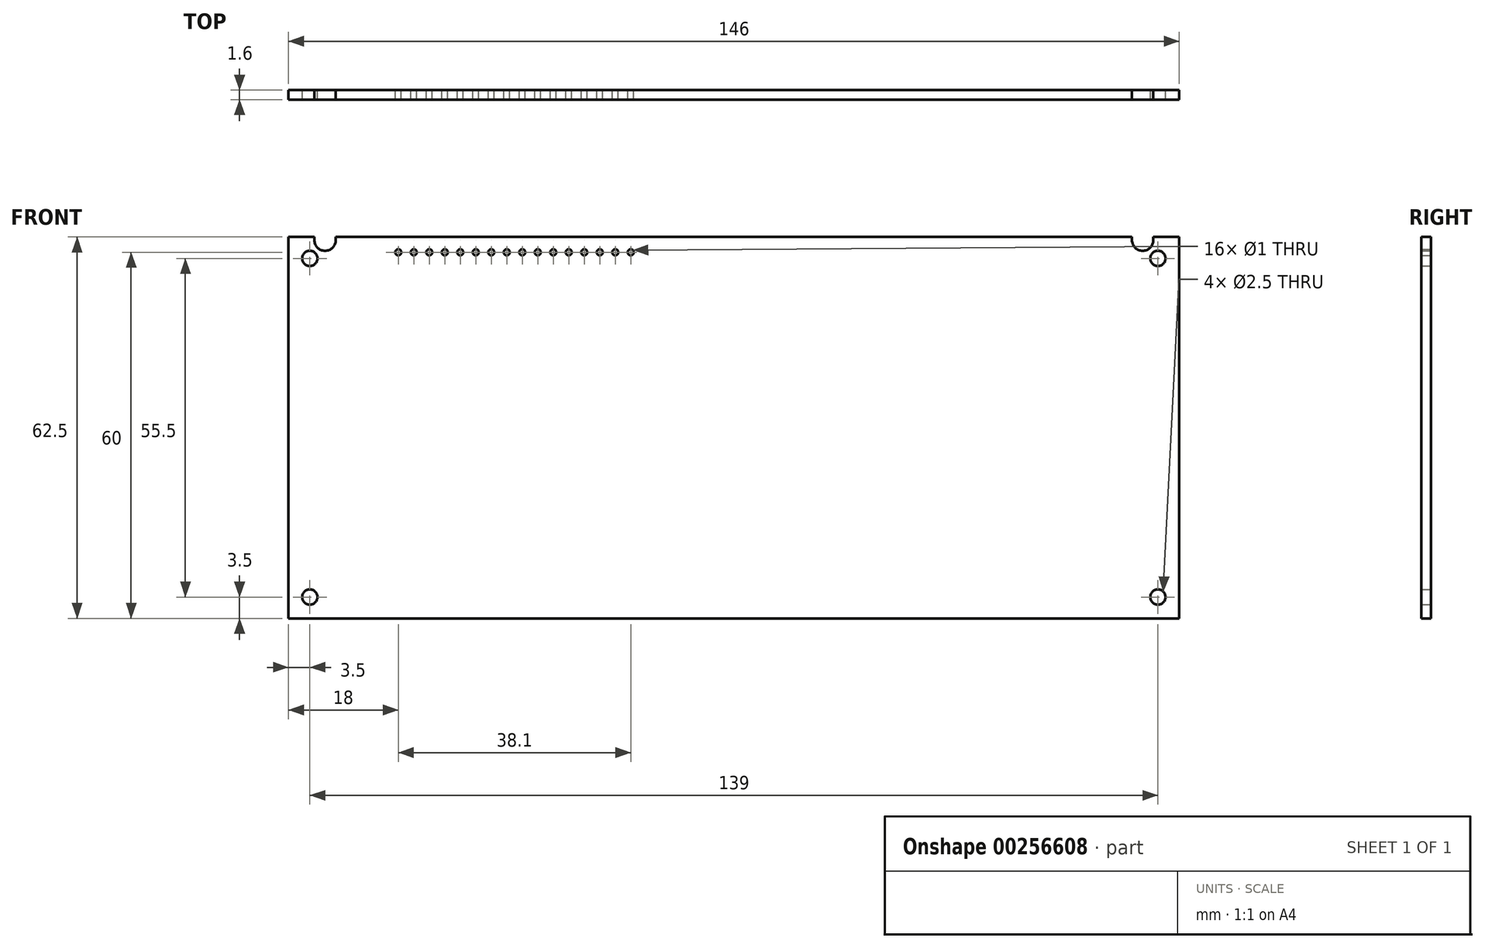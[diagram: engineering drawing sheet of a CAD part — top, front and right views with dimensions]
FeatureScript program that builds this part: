
annotation { "Feature Type Name" : "Feature", "Feature Type Description" : "" }
export const myFeature = defineFeature(function(context is Context, id is Id, definition is map)
    precondition{}
    {
        {
            var Q0;
            Q0=qCreatedBy(makeId("Front.planeOp"),FACE);
            var sketch = newSketch(context, id + "F0", { "sketchPlane" : qUnion([Q0])});
            skLineSegment(sketch, "E0.bottom", {"start": v(73, -31.25) * mm, "end": v(-73, -31.25) * mm});
            skLineSegment(sketch, "E0.top", {"start": v(73, 31.25) * mm, "end": v(-73, 31.25) * mm});
            skLineSegment(sketch, "E0.left", {"start": v(73, -31.25) * mm, "end": v(73, 31.25) * mm});
            skLineSegment(sketch, "E0.right", {"start": v(-73, -31.25) * mm, "end": v(-73, 31.25) * mm});
            skPoint(sketch, "E0.middle", {"position": v(0, 0) * mm});
            skCircle(sketch, "E1", {"center": v(-69.5, -27.75) * mm, "radius": 1.25 * mm});
            skCircle(sketch, "E2", {"center": v(69.5, -27.75) * mm, "radius": 1.25 * mm});
            skCircle(sketch, "E3", {"center": v(69.5, 27.75) * mm, "radius": 1.25 * mm});
            skCircle(sketch, "E4", {"center": v(-69.5, 27.75) * mm, "radius": 1.25 * mm});
            skLineSegment(sketch, "E5.bottom", {"start": v(-67, 29) * mm, "end": v(-67, 29) * mm});
            skLineSegment(sketch, "E5.top", {"start": v(-65.25, 33.5) * mm, "end": v(-68.75, 33.5) * mm});
            skLineSegment(sketch, "E5.left", {"start": v(-65.25, 30.75) * mm, "end": v(-65.25, 33.5) * mm});
            skLineSegment(sketch, "E5.right", {"start": v(-68.75, 30.75) * mm, "end": v(-68.75, 33.5) * mm});
            skPoint(sketch, "E5.middle", {"position": v(-67, 31.25) * mm});
            skLineSegment(sketch, "E6.bottom", {"start": v(67, 29) * mm, "end": v(67, 29) * mm});
            skLineSegment(sketch, "E6.top", {"start": v(68.75, 33.5) * mm, "end": v(65.25, 33.5) * mm});
            skLineSegment(sketch, "E6.left", {"start": v(68.75, 30.75) * mm, "end": v(68.75, 33.5) * mm});
            skLineSegment(sketch, "E6.right", {"start": v(65.25, 30.75) * mm, "end": v(65.25, 33.5) * mm});
            skPoint(sketch, "E6.middle", {"position": v(67, 31.25) * mm});
            skPoint(sketch, "E7.visualSharp", {"position": v(-68.75, 29) * mm});
            skArc(sketch, "E7.filletArc", {"start": v(-68.75, 30.75) * mm, "mid": v(-68.24, 29.51) * mm, "end": v(-67, 29) * mm});
            skPoint(sketch, "E8.visualSharp", {"position": v(-65.25, 29) * mm});
            skArc(sketch, "E8.filletArc", {"start": v(-67, 29) * mm, "mid": v(-65.76, 29.51) * mm, "end": v(-65.25, 30.75) * mm});
            skPoint(sketch, "E9.visualSharp", {"position": v(65.25, 29) * mm});
            skArc(sketch, "E9.filletArc", {"start": v(65.25, 30.75) * mm, "mid": v(65.76, 29.51) * mm, "end": v(67, 29) * mm});
            skPoint(sketch, "E10.visualSharp", {"position": v(68.75, 29) * mm});
            skArc(sketch, "E10.filletArc", {"start": v(67, 29) * mm, "mid": v(68.24, 29.51) * mm, "end": v(68.75, 30.75) * mm});
            skLineSegment(sketch, "E11", {"start": v(-55, 28.75) * mm, "end": v(-16.9, 28.75) * mm, "construction": true});
            skCircle(sketch, "E12", {"center": v(-55, 28.75) * mm, "radius": 0.5 * mm});
            skCircle(sketch, "E13", {"center": v(-52.46, 28.75) * mm, "radius": 0.5 * mm});
            skCircle(sketch, "E14", {"center": v(-47.38, 28.75) * mm, "radius": 0.5 * mm});
            skCircle(sketch, "E15", {"center": v(-49.92, 28.75) * mm, "radius": 0.5 * mm});
            skCircle(sketch, "E16", {"center": v(-37.22, 28.75) * mm, "radius": 0.5 * mm});
            skCircle(sketch, "E17", {"center": v(-39.76, 28.75) * mm, "radius": 0.5 * mm});
            skCircle(sketch, "E18", {"center": v(-44.84, 28.75) * mm, "radius": 0.5 * mm});
            skCircle(sketch, "E19", {"center": v(-42.3, 28.75) * mm, "radius": 0.5 * mm});
            skCircle(sketch, "E20", {"center": v(-34.68, 28.75) * mm, "radius": 0.5 * mm});
            skCircle(sketch, "E21", {"center": v(-32.14, 28.75) * mm, "radius": 0.5 * mm});
            skCircle(sketch, "E22", {"center": v(-29.6, 28.75) * mm, "radius": 0.5 * mm});
            skCircle(sketch, "E23", {"center": v(-21.98, 28.75) * mm, "radius": 0.5 * mm});
            skCircle(sketch, "E24", {"center": v(-24.52, 28.75) * mm, "radius": 0.5 * mm});
            skCircle(sketch, "E25", {"center": v(-27.06, 28.75) * mm, "radius": 0.5 * mm});
            skCircle(sketch, "E26", {"center": v(-19.44, 28.75) * mm, "radius": 0.5 * mm});
            skCircle(sketch, "E27", {"center": v(-16.9, 28.75) * mm, "radius": 0.5 * mm});
            skCircle(sketch, "E28", {"center": v(-69.5, 27.75) * mm, "radius": 2 * mm});
            skCircle(sketch, "E29", {"center": v(69.5, 27.75) * mm, "radius": 2 * mm});
            skCircle(sketch, "E30", {"center": v(69.5, -27.75) * mm, "radius": 2 * mm});
            skCircle(sketch, "E31", {"center": v(-69.5, -27.75) * mm, "radius": 2 * mm});
            skLineSegment(sketch, "E32.bottom", {"start": v(-55, 27.85) * mm, "end": v(-55, 27.85) * mm});
            skLineSegment(sketch, "E32.top", {"start": v(-54.1, 29.65) * mm, "end": v(-55.9, 29.65) * mm, "construction": true});
            skLineSegment(sketch, "E32.left", {"start": v(-54.1, 28.75) * mm, "end": v(-54.1, 29.65) * mm});
            skLineSegment(sketch, "E32.right", {"start": v(-55.9, 28.75) * mm, "end": v(-55.9, 29.65) * mm});
            skPoint(sketch, "E33.visualSharp", {"position": v(-55.9, 27.85) * mm});
            skArc(sketch, "E33.filletArc", {"start": v(-55.9, 28.75) * mm, "mid": v(-55.64, 28.11) * mm, "end": v(-55, 27.85) * mm});
            skPoint(sketch, "E34.visualSharp", {"position": v(-54.1, 27.85) * mm});
            skArc(sketch, "E34.filletArc", {"start": v(-55, 27.85) * mm, "mid": v(-54.36, 28.11) * mm, "end": v(-54.1, 28.75) * mm});
            skLineSegment(sketch, "E35.bottom", {"start": v(-52.46, 27.85) * mm, "end": v(-52.46, 27.85) * mm});
            skLineSegment(sketch, "E35.top", {"start": v(-51.56, 29.65) * mm, "end": v(-53.36, 29.65) * mm, "construction": true});
            skLineSegment(sketch, "E35.left", {"start": v(-51.56, 28.75) * mm, "end": v(-51.56, 29.65) * mm});
            skLineSegment(sketch, "E35.right", {"start": v(-53.36, 28.75) * mm, "end": v(-53.36, 29.65) * mm});
            skPoint(sketch, "E36.visualSharp", {"position": v(-53.36, 27.85) * mm});
            skArc(sketch, "E36.filletArc", {"start": v(-53.36, 28.75) * mm, "mid": v(-53.1, 28.11) * mm, "end": v(-52.46, 27.85) * mm});
            skPoint(sketch, "E37.visualSharp", {"position": v(-51.56, 27.85) * mm});
            skArc(sketch, "E37.filletArc", {"start": v(-52.46, 27.85) * mm, "mid": v(-51.82, 28.11) * mm, "end": v(-51.56, 28.75) * mm});
            skLineSegment(sketch, "E38.bottom", {"start": v(-49.92, 27.85) * mm, "end": v(-49.92, 27.85) * mm});
            skLineSegment(sketch, "E38.top", {"start": v(-49.02, 29.65) * mm, "end": v(-50.82, 29.65) * mm, "construction": true});
            skLineSegment(sketch, "E38.left", {"start": v(-49.02, 28.75) * mm, "end": v(-49.02, 29.65) * mm});
            skLineSegment(sketch, "E38.right", {"start": v(-50.82, 28.75) * mm, "end": v(-50.82, 29.65) * mm});
            skPoint(sketch, "E39.visualSharp", {"position": v(-50.82, 27.85) * mm});
            skArc(sketch, "E39.filletArc", {"start": v(-50.82, 28.75) * mm, "mid": v(-50.56, 28.11) * mm, "end": v(-49.92, 27.85) * mm});
            skPoint(sketch, "E40.visualSharp", {"position": v(-49.02, 27.85) * mm});
            skArc(sketch, "E40.filletArc", {"start": v(-49.92, 27.85) * mm, "mid": v(-49.28, 28.11) * mm, "end": v(-49.02, 28.75) * mm});
            skLineSegment(sketch, "E41.bottom", {"start": v(-44.84, 27.85) * mm, "end": v(-44.84, 27.85) * mm});
            skLineSegment(sketch, "E41.top", {"start": v(-43.94, 29.65) * mm, "end": v(-45.74, 29.65) * mm, "construction": true});
            skLineSegment(sketch, "E41.left", {"start": v(-43.94, 28.75) * mm, "end": v(-43.94, 29.65) * mm});
            skLineSegment(sketch, "E41.right", {"start": v(-45.74, 28.75) * mm, "end": v(-45.74, 29.65) * mm});
            skPoint(sketch, "E42.visualSharp", {"position": v(-45.74, 27.85) * mm});
            skArc(sketch, "E42.filletArc", {"start": v(-45.74, 28.75) * mm, "mid": v(-45.48, 28.11) * mm, "end": v(-44.84, 27.85) * mm});
            skPoint(sketch, "E43.visualSharp", {"position": v(-43.94, 27.85) * mm});
            skArc(sketch, "E43.filletArc", {"start": v(-44.84, 27.85) * mm, "mid": v(-44.2, 28.11) * mm, "end": v(-43.94, 28.75) * mm});
            skLineSegment(sketch, "E44.bottom", {"start": v(-47.38, 27.85) * mm, "end": v(-47.38, 27.85) * mm});
            skLineSegment(sketch, "E44.top", {"start": v(-46.48, 29.65) * mm, "end": v(-48.28, 29.65) * mm, "construction": true});
            skLineSegment(sketch, "E44.left", {"start": v(-46.48, 28.75) * mm, "end": v(-46.48, 29.65) * mm});
            skLineSegment(sketch, "E44.right", {"start": v(-48.28, 28.75) * mm, "end": v(-48.28, 29.65) * mm});
            skPoint(sketch, "E45.visualSharp", {"position": v(-48.28, 27.85) * mm});
            skArc(sketch, "E45.filletArc", {"start": v(-48.28, 28.75) * mm, "mid": v(-48.02, 28.11) * mm, "end": v(-47.38, 27.85) * mm});
            skPoint(sketch, "E46.visualSharp", {"position": v(-46.48, 27.85) * mm});
            skArc(sketch, "E46.filletArc", {"start": v(-47.38, 27.85) * mm, "mid": v(-46.74, 28.11) * mm, "end": v(-46.48, 28.75) * mm});
            skLineSegment(sketch, "E47.bottom", {"start": v(-42.3, 27.85) * mm, "end": v(-42.3, 27.85) * mm});
            skLineSegment(sketch, "E47.top", {"start": v(-41.4, 29.65) * mm, "end": v(-43.2, 29.65) * mm, "construction": true});
            skLineSegment(sketch, "E47.left", {"start": v(-41.4, 28.75) * mm, "end": v(-41.4, 29.65) * mm});
            skLineSegment(sketch, "E47.right", {"start": v(-43.2, 28.75) * mm, "end": v(-43.2, 29.65) * mm});
            skPoint(sketch, "E48.visualSharp", {"position": v(-43.2, 27.85) * mm});
            skArc(sketch, "E48.filletArc", {"start": v(-43.2, 28.75) * mm, "mid": v(-42.94, 28.11) * mm, "end": v(-42.3, 27.85) * mm});
            skPoint(sketch, "E49.visualSharp", {"position": v(-41.4, 27.85) * mm});
            skArc(sketch, "E49.filletArc", {"start": v(-42.3, 27.85) * mm, "mid": v(-41.66, 28.11) * mm, "end": v(-41.4, 28.75) * mm});
            skLineSegment(sketch, "E50.bottom", {"start": v(-39.76, 27.85) * mm, "end": v(-39.76, 27.85) * mm});
            skLineSegment(sketch, "E50.top", {"start": v(-38.86, 29.65) * mm, "end": v(-40.66, 29.65) * mm, "construction": true});
            skLineSegment(sketch, "E50.left", {"start": v(-38.86, 28.75) * mm, "end": v(-38.86, 29.65) * mm});
            skLineSegment(sketch, "E50.right", {"start": v(-40.66, 28.75) * mm, "end": v(-40.66, 29.65) * mm});
            skPoint(sketch, "E51.visualSharp", {"position": v(-40.66, 27.85) * mm});
            skArc(sketch, "E51.filletArc", {"start": v(-40.66, 28.75) * mm, "mid": v(-40.4, 28.11) * mm, "end": v(-39.76, 27.85) * mm});
            skPoint(sketch, "E52.visualSharp", {"position": v(-38.86, 27.85) * mm});
            skArc(sketch, "E52.filletArc", {"start": v(-39.76, 27.85) * mm, "mid": v(-39.12, 28.11) * mm, "end": v(-38.86, 28.75) * mm});
            skLineSegment(sketch, "E53.bottom", {"start": v(-16.9, 27.85) * mm, "end": v(-16.9, 27.85) * mm});
            skLineSegment(sketch, "E53.top", {"start": v(-16, 29.65) * mm, "end": v(-17.8, 29.65) * mm, "construction": true});
            skLineSegment(sketch, "E53.left", {"start": v(-16, 28.75) * mm, "end": v(-16, 29.65) * mm});
            skLineSegment(sketch, "E53.right", {"start": v(-17.8, 28.75) * mm, "end": v(-17.8, 29.65) * mm});
            skPoint(sketch, "E54.visualSharp", {"position": v(-17.8, 27.85) * mm});
            skArc(sketch, "E54.filletArc", {"start": v(-17.8, 28.75) * mm, "mid": v(-17.54, 28.11) * mm, "end": v(-16.9, 27.85) * mm});
            skPoint(sketch, "E55.visualSharp", {"position": v(-16, 27.85) * mm});
            skArc(sketch, "E55.filletArc", {"start": v(-16.9, 27.85) * mm, "mid": v(-16.26, 28.11) * mm, "end": v(-16, 28.75) * mm});
            skLineSegment(sketch, "E56.bottom", {"start": v(-19.44, 27.85) * mm, "end": v(-19.44, 27.85) * mm});
            skLineSegment(sketch, "E56.top", {"start": v(-18.54, 29.65) * mm, "end": v(-20.34, 29.65) * mm, "construction": true});
            skLineSegment(sketch, "E56.left", {"start": v(-18.54, 28.75) * mm, "end": v(-18.54, 29.65) * mm});
            skLineSegment(sketch, "E56.right", {"start": v(-20.34, 28.75) * mm, "end": v(-20.34, 29.65) * mm});
            skPoint(sketch, "E57.visualSharp", {"position": v(-20.34, 27.85) * mm});
            skArc(sketch, "E57.filletArc", {"start": v(-20.34, 28.75) * mm, "mid": v(-20.08, 28.11) * mm, "end": v(-19.44, 27.85) * mm});
            skPoint(sketch, "E58.visualSharp", {"position": v(-18.54, 27.85) * mm});
            skArc(sketch, "E58.filletArc", {"start": v(-19.44, 27.85) * mm, "mid": v(-18.8, 28.11) * mm, "end": v(-18.54, 28.75) * mm});
            skLineSegment(sketch, "E59.bottom", {"start": v(-21.98, 27.85) * mm, "end": v(-21.98, 27.85) * mm});
            skLineSegment(sketch, "E59.top", {"start": v(-21.08, 29.65) * mm, "end": v(-22.88, 29.65) * mm, "construction": true});
            skLineSegment(sketch, "E59.left", {"start": v(-21.08, 28.75) * mm, "end": v(-21.08, 29.65) * mm});
            skLineSegment(sketch, "E59.right", {"start": v(-22.88, 28.75) * mm, "end": v(-22.88, 29.65) * mm});
            skPoint(sketch, "E60.visualSharp", {"position": v(-22.88, 27.85) * mm});
            skArc(sketch, "E60.filletArc", {"start": v(-22.88, 28.75) * mm, "mid": v(-22.62, 28.11) * mm, "end": v(-21.98, 27.85) * mm});
            skPoint(sketch, "E61.visualSharp", {"position": v(-21.08, 27.85) * mm});
            skArc(sketch, "E61.filletArc", {"start": v(-21.98, 27.85) * mm, "mid": v(-21.34, 28.11) * mm, "end": v(-21.08, 28.75) * mm});
            skLineSegment(sketch, "E62.bottom", {"start": v(-24.52, 27.85) * mm, "end": v(-24.52, 27.85) * mm});
            skLineSegment(sketch, "E62.top", {"start": v(-23.62, 29.65) * mm, "end": v(-25.42, 29.65) * mm, "construction": true});
            skLineSegment(sketch, "E62.left", {"start": v(-23.62, 28.75) * mm, "end": v(-23.62, 29.65) * mm});
            skLineSegment(sketch, "E62.right", {"start": v(-25.42, 28.75) * mm, "end": v(-25.42, 29.65) * mm});
            skPoint(sketch, "E63.visualSharp", {"position": v(-25.42, 27.85) * mm});
            skArc(sketch, "E63.filletArc", {"start": v(-25.42, 28.75) * mm, "mid": v(-25.16, 28.11) * mm, "end": v(-24.52, 27.85) * mm});
            skPoint(sketch, "E64.visualSharp", {"position": v(-23.62, 27.85) * mm});
            skArc(sketch, "E64.filletArc", {"start": v(-24.52, 27.85) * mm, "mid": v(-23.88, 28.11) * mm, "end": v(-23.62, 28.75) * mm});
            skLineSegment(sketch, "E65.bottom", {"start": v(-27.06, 27.85) * mm, "end": v(-27.06, 27.85) * mm});
            skLineSegment(sketch, "E65.top", {"start": v(-26.16, 29.65) * mm, "end": v(-27.96, 29.65) * mm, "construction": true});
            skLineSegment(sketch, "E65.left", {"start": v(-26.16, 28.75) * mm, "end": v(-26.16, 29.65) * mm});
            skLineSegment(sketch, "E65.right", {"start": v(-27.96, 28.75) * mm, "end": v(-27.96, 29.65) * mm});
            skPoint(sketch, "E66.visualSharp", {"position": v(-27.96, 27.85) * mm});
            skArc(sketch, "E66.filletArc", {"start": v(-27.96, 28.75) * mm, "mid": v(-27.7, 28.11) * mm, "end": v(-27.06, 27.85) * mm});
            skPoint(sketch, "E67.visualSharp", {"position": v(-26.16, 27.85) * mm});
            skArc(sketch, "E67.filletArc", {"start": v(-27.06, 27.85) * mm, "mid": v(-26.42, 28.11) * mm, "end": v(-26.16, 28.75) * mm});
            skLineSegment(sketch, "E68.bottom", {"start": v(-29.6, 27.85) * mm, "end": v(-29.6, 27.85) * mm});
            skLineSegment(sketch, "E68.top", {"start": v(-28.7, 29.65) * mm, "end": v(-30.5, 29.65) * mm, "construction": true});
            skLineSegment(sketch, "E68.left", {"start": v(-28.7, 28.75) * mm, "end": v(-28.7, 29.65) * mm});
            skLineSegment(sketch, "E68.right", {"start": v(-30.5, 28.75) * mm, "end": v(-30.5, 29.65) * mm});
            skPoint(sketch, "E69.visualSharp", {"position": v(-30.5, 27.85) * mm});
            skArc(sketch, "E69.filletArc", {"start": v(-30.5, 28.75) * mm, "mid": v(-30.24, 28.11) * mm, "end": v(-29.6, 27.85) * mm});
            skPoint(sketch, "E70.visualSharp", {"position": v(-28.7, 27.85) * mm});
            skArc(sketch, "E70.filletArc", {"start": v(-29.6, 27.85) * mm, "mid": v(-28.96, 28.11) * mm, "end": v(-28.7, 28.75) * mm});
            skLineSegment(sketch, "E71.bottom", {"start": v(-32.14, 27.85) * mm, "end": v(-32.14, 27.85) * mm});
            skLineSegment(sketch, "E71.top", {"start": v(-31.24, 29.65) * mm, "end": v(-33.04, 29.65) * mm, "construction": true});
            skLineSegment(sketch, "E71.left", {"start": v(-31.24, 28.75) * mm, "end": v(-31.24, 29.65) * mm});
            skLineSegment(sketch, "E71.right", {"start": v(-33.04, 28.75) * mm, "end": v(-33.04, 29.65) * mm});
            skPoint(sketch, "E72.visualSharp", {"position": v(-33.04, 27.85) * mm});
            skArc(sketch, "E72.filletArc", {"start": v(-33.04, 28.75) * mm, "mid": v(-32.78, 28.11) * mm, "end": v(-32.14, 27.85) * mm});
            skPoint(sketch, "E73.visualSharp", {"position": v(-31.24, 27.85) * mm});
            skArc(sketch, "E73.filletArc", {"start": v(-32.14, 27.85) * mm, "mid": v(-31.5, 28.11) * mm, "end": v(-31.24, 28.75) * mm});
            skLineSegment(sketch, "E74.bottom", {"start": v(-34.68, 27.85) * mm, "end": v(-34.68, 27.85) * mm});
            skLineSegment(sketch, "E74.top", {"start": v(-33.78, 29.65) * mm, "end": v(-35.58, 29.65) * mm, "construction": true});
            skLineSegment(sketch, "E74.left", {"start": v(-33.78, 28.75) * mm, "end": v(-33.78, 29.65) * mm});
            skLineSegment(sketch, "E74.right", {"start": v(-35.58, 28.75) * mm, "end": v(-35.58, 29.65) * mm});
            skPoint(sketch, "E75.visualSharp", {"position": v(-35.58, 27.85) * mm});
            skArc(sketch, "E75.filletArc", {"start": v(-35.58, 28.75) * mm, "mid": v(-35.32, 28.11) * mm, "end": v(-34.68, 27.85) * mm});
            skPoint(sketch, "E76.visualSharp", {"position": v(-33.78, 27.85) * mm});
            skArc(sketch, "E76.filletArc", {"start": v(-34.68, 27.85) * mm, "mid": v(-34.04, 28.11) * mm, "end": v(-33.78, 28.75) * mm});
            skLineSegment(sketch, "E77.bottom", {"start": v(-37.22, 27.85) * mm, "end": v(-37.22, 27.85) * mm});
            skLineSegment(sketch, "E77.top", {"start": v(-36.32, 29.65) * mm, "end": v(-38.12, 29.65) * mm, "construction": true});
            skLineSegment(sketch, "E77.left", {"start": v(-36.32, 28.75) * mm, "end": v(-36.32, 29.65) * mm});
            skLineSegment(sketch, "E77.right", {"start": v(-38.12, 28.75) * mm, "end": v(-38.12, 29.65) * mm});
            skPoint(sketch, "E78.visualSharp", {"position": v(-38.12, 27.85) * mm});
            skArc(sketch, "E78.filletArc", {"start": v(-38.12, 28.75) * mm, "mid": v(-37.86, 28.11) * mm, "end": v(-37.22, 27.85) * mm});
            skPoint(sketch, "E79.visualSharp", {"position": v(-36.32, 27.85) * mm});
            skArc(sketch, "E79.filletArc", {"start": v(-37.22, 27.85) * mm, "mid": v(-36.58, 28.11) * mm, "end": v(-36.32, 28.75) * mm});
            skLineSegment(sketch, "E80", {"start": v(-55.9, 29.65) * mm, "end": v(-55.9, 31.25) * mm});
            skLineSegment(sketch, "E81", {"start": v(-54.1, 29.65) * mm, "end": v(-54.1, 31.25) * mm});
            skLineSegment(sketch, "E82", {"start": v(-53.36, 29.65) * mm, "end": v(-53.36, 31.25) * mm});
            skLineSegment(sketch, "E83", {"start": v(-51.56, 29.65) * mm, "end": v(-51.56, 31.25) * mm});
            skLineSegment(sketch, "E84", {"start": v(-50.82, 29.65) * mm, "end": v(-50.82, 31.25) * mm});
            skLineSegment(sketch, "E85", {"start": v(-49.02, 29.65) * mm, "end": v(-49.02, 31.25) * mm});
            skLineSegment(sketch, "E86", {"start": v(-48.28, 29.65) * mm, "end": v(-48.28, 31.25) * mm});
            skLineSegment(sketch, "E87", {"start": v(-46.48, 29.65) * mm, "end": v(-46.48, 31.25) * mm});
            skLineSegment(sketch, "E88", {"start": v(-45.74, 29.65) * mm, "end": v(-45.74, 31.25) * mm});
            skLineSegment(sketch, "E89", {"start": v(-43.94, 29.65) * mm, "end": v(-43.94, 31.25) * mm});
            skLineSegment(sketch, "E90", {"start": v(-43.2, 29.65) * mm, "end": v(-43.2, 31.25) * mm});
            skLineSegment(sketch, "E91", {"start": v(-41.4, 29.65) * mm, "end": v(-41.4, 31.25) * mm});
            skLineSegment(sketch, "E92", {"start": v(-40.66, 29.65) * mm, "end": v(-40.66, 31.25) * mm});
            skLineSegment(sketch, "E93", {"start": v(-38.86, 29.65) * mm, "end": v(-38.86, 31.25) * mm});
            skLineSegment(sketch, "E94", {"start": v(-38.12, 29.65) * mm, "end": v(-38.12, 31.25) * mm});
            skLineSegment(sketch, "E95", {"start": v(-36.32, 29.65) * mm, "end": v(-36.32, 31.25) * mm});
            skLineSegment(sketch, "E96", {"start": v(-35.58, 29.65) * mm, "end": v(-35.58, 31.25) * mm});
            skLineSegment(sketch, "E97", {"start": v(-33.78, 29.65) * mm, "end": v(-33.78, 31.25) * mm});
            skLineSegment(sketch, "E98", {"start": v(-33.04, 29.65) * mm, "end": v(-33.04, 31.25) * mm});
            skLineSegment(sketch, "E99", {"start": v(-31.24, 29.65) * mm, "end": v(-31.24, 31.25) * mm});
            skLineSegment(sketch, "E100", {"start": v(-30.5, 29.65) * mm, "end": v(-30.5, 31.25) * mm});
            skLineSegment(sketch, "E101", {"start": v(-28.7, 29.65) * mm, "end": v(-28.7, 31.25) * mm});
            skLineSegment(sketch, "E102", {"start": v(-27.96, 29.65) * mm, "end": v(-27.96, 31.25) * mm});
            skLineSegment(sketch, "E103", {"start": v(-26.16, 29.65) * mm, "end": v(-26.16, 31.25) * mm});
            skLineSegment(sketch, "E104", {"start": v(-25.42, 29.65) * mm, "end": v(-25.42, 31.25) * mm});
            skLineSegment(sketch, "E105", {"start": v(-23.62, 29.65) * mm, "end": v(-23.62, 31.25) * mm});
            skLineSegment(sketch, "E106", {"start": v(-22.88, 29.65) * mm, "end": v(-22.88, 31.25) * mm});
            skLineSegment(sketch, "E107", {"start": v(-21.08, 29.65) * mm, "end": v(-21.08, 31.25) * mm});
            skLineSegment(sketch, "E108", {"start": v(-20.34, 29.65) * mm, "end": v(-20.34, 31.25) * mm});
            skLineSegment(sketch, "E109", {"start": v(-18.54, 29.65) * mm, "end": v(-18.54, 31.25) * mm});
            skLineSegment(sketch, "E110", {"start": v(-17.8, 29.65) * mm, "end": v(-17.8, 31.25) * mm});
            skLineSegment(sketch, "E111", {"start": v(-16, 29.65) * mm, "end": v(-16, 31.25) * mm});
            skSolve(sketch);
        }
        {
            var Q0;
            Q0=makeQuery(id+"F0.imprint","IMPRINT",FACE,{"disambiguationData":[TD([[makeQuery(id+"F0.imprint","IMPRINT",EDGE,{"derivedFrom":sQuery(id+"F0.wireOp",EDGE,"E0.bottom")}),-1.0]])]});
            var Q1;
            Q1=makeQuery(id+"F0.imprint","IMPRINT",FACE,{"disambiguationData":[TD([[makeQuery(id+"F0.imprint","IMPRINT",EDGE,{"derivedFrom":sQuery(id+"F0.wireOp",EDGE,"E4")}),-1.0]])]});
            var Q2;
            Q2=makeQuery(id+"F0.imprint","IMPRINT",FACE,{"disambiguationData":[TD([[makeQuery(id+"F0.imprint","IMPRINT",EDGE,{"derivedFrom":sQuery(id+"F0.wireOp",EDGE,"E1")}),-1.0]])]});
            var Q3;
            Q3=makeQuery(id+"F0.imprint","IMPRINT",FACE,{"disambiguationData":[TD([[makeQuery(id+"F0.imprint","IMPRINT",EDGE,{"derivedFrom":sQuery(id+"F0.wireOp",EDGE,"E3")}),-1.0]])]});
            var Q4;
            Q4=makeQuery(id+"F0.imprint","IMPRINT",FACE,{"disambiguationData":[TD([[makeQuery(id+"F0.imprint","IMPRINT",EDGE,{"derivedFrom":sQuery(id+"F0.wireOp",EDGE,"E2")}),-1.0]])]});
            var Q5;
            Q5=makeQuery(id+"F0.imprint","IMPRINT",FACE,{"disambiguationData":[TD([[makeQuery(id+"F0.imprint","IMPRINT",EDGE,{"derivedFrom":sQuery(id+"F0.wireOp",EDGE,"E12")}),-1.0]])]});
            var Q6;
            Q6=makeQuery(id+"F0.imprint","IMPRINT",FACE,{"disambiguationData":[TD([[makeQuery(id+"F0.imprint","IMPRINT",EDGE,{"derivedFrom":sQuery(id+"F0.wireOp",EDGE,"E13")}),-1.0]])]});
            var Q7;
            Q7=makeQuery(id+"F0.imprint","IMPRINT",FACE,{"disambiguationData":[TD([[makeQuery(id+"F0.imprint","IMPRINT",EDGE,{"derivedFrom":sQuery(id+"F0.wireOp",EDGE,"E15")}),-1.0]])]});
            var Q8;
            Q8=makeQuery(id+"F0.imprint","IMPRINT",FACE,{"disambiguationData":[TD([[makeQuery(id+"F0.imprint","IMPRINT",EDGE,{"derivedFrom":sQuery(id+"F0.wireOp",EDGE,"E14")}),-1.0]])]});
            var Q9;
            Q9=makeQuery(id+"F0.imprint","IMPRINT",FACE,{"disambiguationData":[TD([[makeQuery(id+"F0.imprint","IMPRINT",EDGE,{"derivedFrom":sQuery(id+"F0.wireOp",EDGE,"E18")}),-1.0]])]});
            var Q10;
            Q10=makeQuery(id+"F0.imprint","IMPRINT",FACE,{"disambiguationData":[TD([[makeQuery(id+"F0.imprint","IMPRINT",EDGE,{"derivedFrom":sQuery(id+"F0.wireOp",EDGE,"E19")}),-1.0]])]});
            var Q11;
            Q11=makeQuery(id+"F0.imprint","IMPRINT",FACE,{"disambiguationData":[TD([[makeQuery(id+"F0.imprint","IMPRINT",EDGE,{"derivedFrom":sQuery(id+"F0.wireOp",EDGE,"E17")}),-1.0]])]});
            var Q12;
            Q12=makeQuery(id+"F0.imprint","IMPRINT",FACE,{"disambiguationData":[TD([[makeQuery(id+"F0.imprint","IMPRINT",EDGE,{"derivedFrom":sQuery(id+"F0.wireOp",EDGE,"E16")}),-1.0]])]});
            var Q13;
            Q13=makeQuery(id+"F0.imprint","IMPRINT",FACE,{"disambiguationData":[TD([[makeQuery(id+"F0.imprint","IMPRINT",EDGE,{"derivedFrom":sQuery(id+"F0.wireOp",EDGE,"E20")}),-1.0]])]});
            var Q14;
            Q14=makeQuery(id+"F0.imprint","IMPRINT",FACE,{"disambiguationData":[TD([[makeQuery(id+"F0.imprint","IMPRINT",EDGE,{"derivedFrom":sQuery(id+"F0.wireOp",EDGE,"E21")}),-1.0]])]});
            var Q15;
            Q15=makeQuery(id+"F0.imprint","IMPRINT",FACE,{"disambiguationData":[TD([[makeQuery(id+"F0.imprint","IMPRINT",EDGE,{"derivedFrom":sQuery(id+"F0.wireOp",EDGE,"E22")}),-1.0]])]});
            var Q16;
            Q16=makeQuery(id+"F0.imprint","IMPRINT",FACE,{"disambiguationData":[TD([[makeQuery(id+"F0.imprint","IMPRINT",EDGE,{"derivedFrom":sQuery(id+"F0.wireOp",EDGE,"E25")}),-1.0]])]});
            var Q17;
            Q17=makeQuery(id+"F0.imprint","IMPRINT",FACE,{"disambiguationData":[TD([[makeQuery(id+"F0.imprint","IMPRINT",EDGE,{"derivedFrom":sQuery(id+"F0.wireOp",EDGE,"E24")}),-1.0]])]});
            var Q18;
            Q18=makeQuery(id+"F0.imprint","IMPRINT",FACE,{"disambiguationData":[TD([[makeQuery(id+"F0.imprint","IMPRINT",EDGE,{"derivedFrom":sQuery(id+"F0.wireOp",EDGE,"E23")}),-1.0]])]});
            var Q19;
            Q19=makeQuery(id+"F0.imprint","IMPRINT",FACE,{"disambiguationData":[TD([[makeQuery(id+"F0.imprint","IMPRINT",EDGE,{"derivedFrom":sQuery(id+"F0.wireOp",EDGE,"E26")}),-1.0]])]});
            var Q20;
            Q20=makeQuery(id+"F0.imprint","IMPRINT",FACE,{"disambiguationData":[TD([[makeQuery(id+"F0.imprint","IMPRINT",EDGE,{"derivedFrom":sQuery(id+"F0.wireOp",EDGE,"E27")}),-1.0]])]});
            extrude(context, id + "F1", {"entities" : qUnion([Q0, Q1, Q2, Q3, Q4, Q5, Q6, Q7, Q8, Q9, Q10, Q11, Q12, Q13, Q14, Q15, Q16, Q17, Q18, Q19, Q20]), "depth" : 1.6 * mm});
        }
    });
